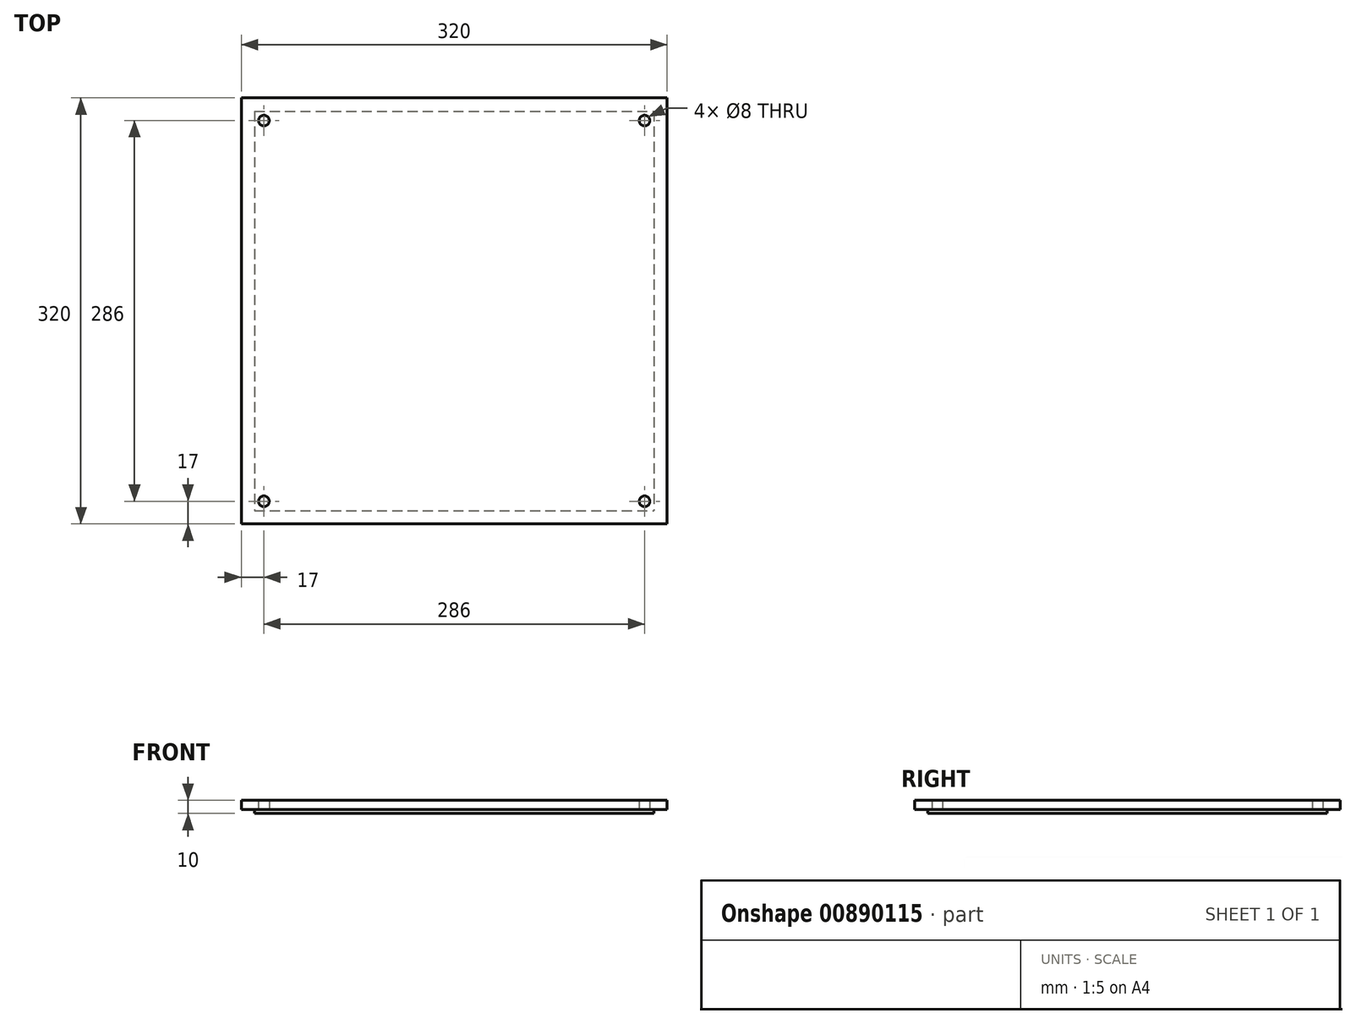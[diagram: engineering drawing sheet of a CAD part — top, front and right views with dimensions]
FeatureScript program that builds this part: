
annotation { "Feature Type Name" : "Feature", "Feature Type Description" : "" }
export const myFeature = defineFeature(function(context is Context, id is Id, definition is map)
    precondition{}
    {
        {
            var Q0;
            Q0=qCreatedBy(makeId("Top.planeOp"),FACE);
            var sketch = newSketch(context, id + "F0", { "sketchPlane" : qUnion([Q0])});
            skLineSegment(sketch, "E0.bottom", {"start": v(-150, 150) * mm, "end": v(150, 150) * mm});
            skLineSegment(sketch, "E0.top", {"start": v(-150, -150) * mm, "end": v(150, -150) * mm});
            skLineSegment(sketch, "E0.left", {"start": v(-150, 150) * mm, "end": v(-150, -150) * mm});
            skLineSegment(sketch, "E0.right", {"start": v(150, 150) * mm, "end": v(150, -150) * mm});
            skPoint(sketch, "E0.middle", {"position": v(0, 0) * mm});
            skLineSegment(sketch, "E1.left", {"start": v(-150, 150) * mm, "end": v(-150, 150) * mm});
            skLineSegment(sketch, "E1.right", {"start": v(150, 150) * mm, "end": v(150, 150) * mm});
            skLineSegment(sketch, "E2.bottom", {"start": v(-160, 160) * mm, "end": v(160, 160) * mm});
            skLineSegment(sketch, "E2.top", {"start": v(-160, -160) * mm, "end": v(160, -160) * mm});
            skLineSegment(sketch, "E2.left", {"start": v(-160, 160) * mm, "end": v(-160, -160) * mm});
            skLineSegment(sketch, "E2.right", {"start": v(160, 160) * mm, "end": v(160, -160) * mm});
            skSolve(sketch);
        }
        {
            var Q0;
            Q0=makeQuery(id+"F0.imprint","IMPRINT",FACE,{"disambiguationData":[TD([[makeQuery(id+"F0.imprint","IMPRINT",EDGE,{"derivedFrom":sQuery(id+"F0.wireOp",EDGE,"E0.top")}),-1.0]])]});
            var Q1;
            Q1=makeQuery(id+"F0.imprint","IMPRINT",FACE,{"disambiguationData":[TD([[makeQuery(id+"F0.imprint","IMPRINT",EDGE,{"derivedFrom":sQuery(id+"F0.wireOp",EDGE,"E0.top")}),1.0]])]});
            extrude(context, id + "F1", {"entities" : qUnion([Q0, Q1]), "depth" : 7 * mm, "offsetDistance" : 25 * mm});
        }
        {
            var Q0;
            Q0=makeQuery(id+"F0.imprint","IMPRINT",FACE,{"disambiguationData":[TD([[makeQuery(id+"F0.imprint","IMPRINT",EDGE,{"derivedFrom":sQuery(id+"F0.wireOp",EDGE,"E0.top")}),1.0]])]});
            extrude(context, id + "F2", {"entities" : qUnion([Q0]), "operationType" : NewBodyOperationType.ADD, "oppositeDirection" : true, "depth" : 3 * mm, "offsetDistance" : 25 * mm});
        }
        {
            var Q0;
            Q0=qCreatedBy(makeId("Top.planeOp"),FACE);
            var sketch = newSketch(context, id + "F3", { "sketchPlane" : qUnion([Q0])});
            skCircle(sketch, "E3", {"center": v(-143, 143) * mm, "radius": 4 * mm});
            skCircle(sketch, "E4.MirrorC", {"center": v(143, 143) * mm, "radius": 4 * mm});
            skCircle(sketch, "E5.MirrorC", {"center": v(143, -143) * mm, "radius": 4 * mm});
            skCircle(sketch, "E6.MirrorC", {"center": v(-143, -143) * mm, "radius": 4 * mm});
            skSolve(sketch);
        }
        {
            var Q0;
            Q0=qSketchRegion(id+"F3",true);
            extrude(context, id + "F4", {"entities" : qUnion([Q0]), "operationType" : NewBodyOperationType.REMOVE, "depth" : 15 * mm, "offsetDistance" : 25 * mm, "symmetric" : true});
        }
    });
